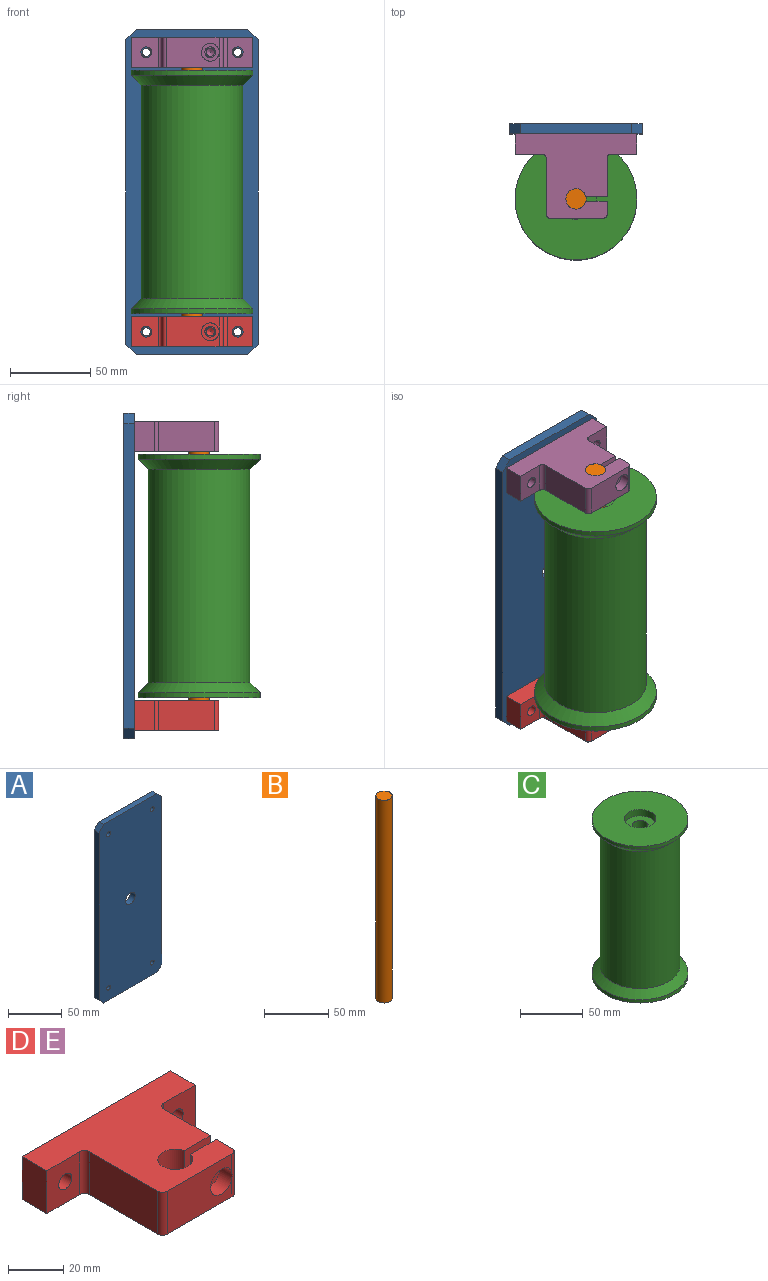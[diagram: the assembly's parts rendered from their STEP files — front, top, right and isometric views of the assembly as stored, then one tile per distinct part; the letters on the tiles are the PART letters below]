
ASSEMBLY  parts=5 mates=4
PART A: 15 faces, bbox 82.6x6.4x203.2 mm
  f0: plane 190.5x6.35mm, normal (1,0,0), area 1209.7mm2, adj f4,f5,f7,f9
  f1: plane 69.85x6.35mm, normal (0,0,1), area 443.5mm2, adj f4,f5,f8,f9
  f2: plane 190.5x6.35mm, normal (-1,0,0), area 1209.7mm2, adj f4,f5,f6,f8
  f3: plane 69.85x6.35mm, normal (0,0,-1), area 443.5mm2, adj f4,f5,f6,f7
  f4: plane 203.2x82.55mm, normal (0,-1,0), area 16485mm2, adj f0,f1,f2,f3,f6,f7,f8,f9
  f5: plane 203.2x82.55mm, normal (0,1,0), area 16485mm2, adj f0,f1,f2,f3,f6,f7,f8,f9
  f6: plane 6.35x6.35mm, normal (-0.71,0,-0.71), area 57mm2, adj f2,f3,f4,f5
  f7: plane 6.35x6.35mm, normal (0.71,0,-0.71), area 57mm2, adj f0,f3,f4,f5
  f8: plane 6.35x6.35mm, normal (-0.71,0,0.71), area 57mm2, adj f1,f2,f4,f5
  f9: plane 6.35x6.35mm, normal (0.71,0,0.71), area 57mm2, adj f0,f1,f4,f5
  f10: cylinder r=2.55mm len=6.35mm, axis (0,-1,0), area 101.8mm2, adj f4,f5
  f11: cylinder r=2.55mm len=6.35mm, axis (0,-1,0), area 101.8mm2, adj f4,f5
  f12: cylinder r=2.55mm len=6.35mm, axis (0,-1,0), area 101.8mm2, adj f4,f5
  f13: cylinder r=2.55mm len=6.35mm, axis (0,-1,0), area 101.8mm2, adj f4,f5
  f14: cylinder r=6.35mm len=12.7mm, axis (0,-1,0), area 253.4mm2, adj f4,f5
PART B: 3 faces, bbox 12.7x12.7x193.7 mm
  f0: cylinder r=6.35mm len=193.68mm, axis (0,0,-1), area 7727.3mm2, adj f1,f2
  f1: plane 12.7x12.7mm, normal (0,0,1), area 126.7mm2, adj f0
  f2: plane 12.7x12.7mm, normal (0,0,-1), area 126.7mm2, adj f0
PART C: 12 faces, bbox 76.2x76.2x152.4 mm
  f0: cylinder r=12.7mm len=25.4mm, axis (0,0,1), area 506.7mm2, adj f1,f10
  f1: plane 76.2x76.2mm, normal (0,0,1), area 4053.7mm2, adj f0,f2
  f2: cylinder r=38.1mm len=76.2mm, axis (0,0,1), area 760.1mm2, adj f1,f3
  f3: cone r=38.1mm half-angle=45deg, axis (0,0,1), area 1970.6mm2, adj f2,f4
  f4: cylinder r=31.75mm len=133.35mm, axis (0,0,1), area 26602.1mm2, adj f3,f5
  f5: cone r=38.1mm half-angle=45deg, axis (0,0,-1), area 1970.6mm2, adj f4,f6
  f6: cylinder r=38.1mm len=76.2mm, axis (0,0,1), area 760.1mm2, adj f5,f7
  f7: plane 76.2x76.2mm, normal (0,0,-1), area 4053.7mm2, adj f6,f8
  f8: cylinder r=12.7mm len=25.4mm, axis (0,0,1), area 506.7mm2, adj f7,f9
  f9: plane 25.4x25.4mm, normal (0,0,-1), area 380mm2, adj f8,f11
  f10: plane 25.4x25.4mm, normal (0,0,1), area 380mm2, adj f0,f11
  f11: cylinder r=6.35mm len=139.7mm, axis (0,0,1), area 5573.8mm2, adj f9,f10
PART D: 25 faces, bbox 76.2x52.8x19.1 mm
  f0: plane 23.81x19.05mm, normal (1,0,0), area 453.6mm2, adj f1,f2,f14,f19
  f1: plane 76.2x52.79mm, normal (0,0,1), area 2326.8mm2, adj f0,f3,f4,f5,f6,f7,f8,f9
  f2: plane 76.2x52.79mm, normal (0,0,-1), area 2326.8mm2, adj f0,f3,f4,f5,f6,f7,f8,f9
  f3: plane 19.05x12.7mm, normal (1,0,0), area 241.9mm2, adj f1,f2,f4,f11
  f4: plane 76.2x19.05mm, normal (0,1,0), area 1379.9mm2, adj f1,f2,f3,f5,f12,f13
  f5: plane 19.05x12.7mm, normal (-1,0,0), area 241.9mm2, adj f1,f2,f4,f6
  f6: plane 19.05x16.9mm, normal (0,-1,0), area 286.2mm2, adj f1,f2,f5,f13,f16
  f7: plane 35.01x19.05mm, normal (-1,0,0), area 667mm2, adj f1,f2,f16,f17
  f8: plane 33.03x19.06mm, normal (0,-1,0), area 532.1mm2, adj f1,f2,f17,f18,f22
  f9: plane 19.05x8.02mm, normal (1,0,0), area 152.9mm2, adj f1,f2,f15,f18
  f10: cylinder r=6.35mm len=19.05mm, axis (0,0,-1), area 698.9mm2, adj f1,f2,f14,f15
  f11: plane 19.05x16.12mm, normal (0,-1,0), area 271.2mm2, adj f1,f2,f3,f12,f19
  f12: cylinder r=3.38mm len=12.7mm, axis (0,1,0), area 269.6mm2, adj f4,f11
  f13: cylinder r=3.38mm len=12.7mm, axis (0,1,0), area 269.6mm2, adj f4,f6
  f14: plane 19.05x13.3mm, normal (0,-1,0), area 232.8mm2, adj f0,f1,f2,f10,f23
  f15: plane 19.05x13.3mm, normal (0,1,0), area 217.4mm2, adj f1,f2,f9,f10,f20
  f16: cylinder r=2.54mm len=19.05mm, axis (0,0,1), area 76mm2, adj f1,f2,f6,f7
  f17: cylinder r=2.54mm len=19.05mm, axis (0,0,1), area 76mm2, adj f1,f2,f7,f8
  f18: cylinder r=2.54mm len=19.05mm, axis (0,0,-1), area 75.9mm2, adj f1,f2,f8,f9,f22
  f19: cylinder r=2.54mm len=19.05mm, axis (0,0,-1), area 76mm2, adj f0,f1,f2,f11
  f20: cylinder r=3.38mm len=6.76mm, axis (0,-1,0), area 89.5mm2, adj f15,f21
  f21: plane 11.11x11.11mm, normal (0,-1,0), area 61.1mm2, adj f20,f22
  f22: cylinder r=5.56mm len=11.11mm, axis (0,-1,0), area 221.7mm2, adj f8,f18,f21
  f23: cylinder r=2.55mm len=11.66mm, axis (0,-1,0), area 187mm2, adj f14,f24
  f24: cone r=0mm half-angle=59deg, axis (0,-1,0), area 23.9mm2, adj f23
PART E: same geometry as D
PLACE A t=(-0.86,2.92,0.36)mm fixed
PLACE B t=(-0.86,-44.07,0.36)mm
PLACE C t=(-0.86,-44.07,0.36)mm
PLACE D t=(-0.86,-9.78,-86.95)mm
PLACE E t=(-0.86,-9.78,87.67)mm
MATE fastened B.f0 <-> E.f10  axis (0,0,1) through (-0.86,-44.07,97.2)mm
MATE fastened E.f13 <-> A.f10  axis (0,1,0) through (-29.43,-3.43,87.67)mm
MATE fastened A.f13 <-> D.f13  axis (0,-1,0) through (-29.43,-3.43,-86.95)mm
MATE cylindrical C.f0 <-> B.f0  axis (0,0,1) through (-0.86,-44.07,0.36)mm
